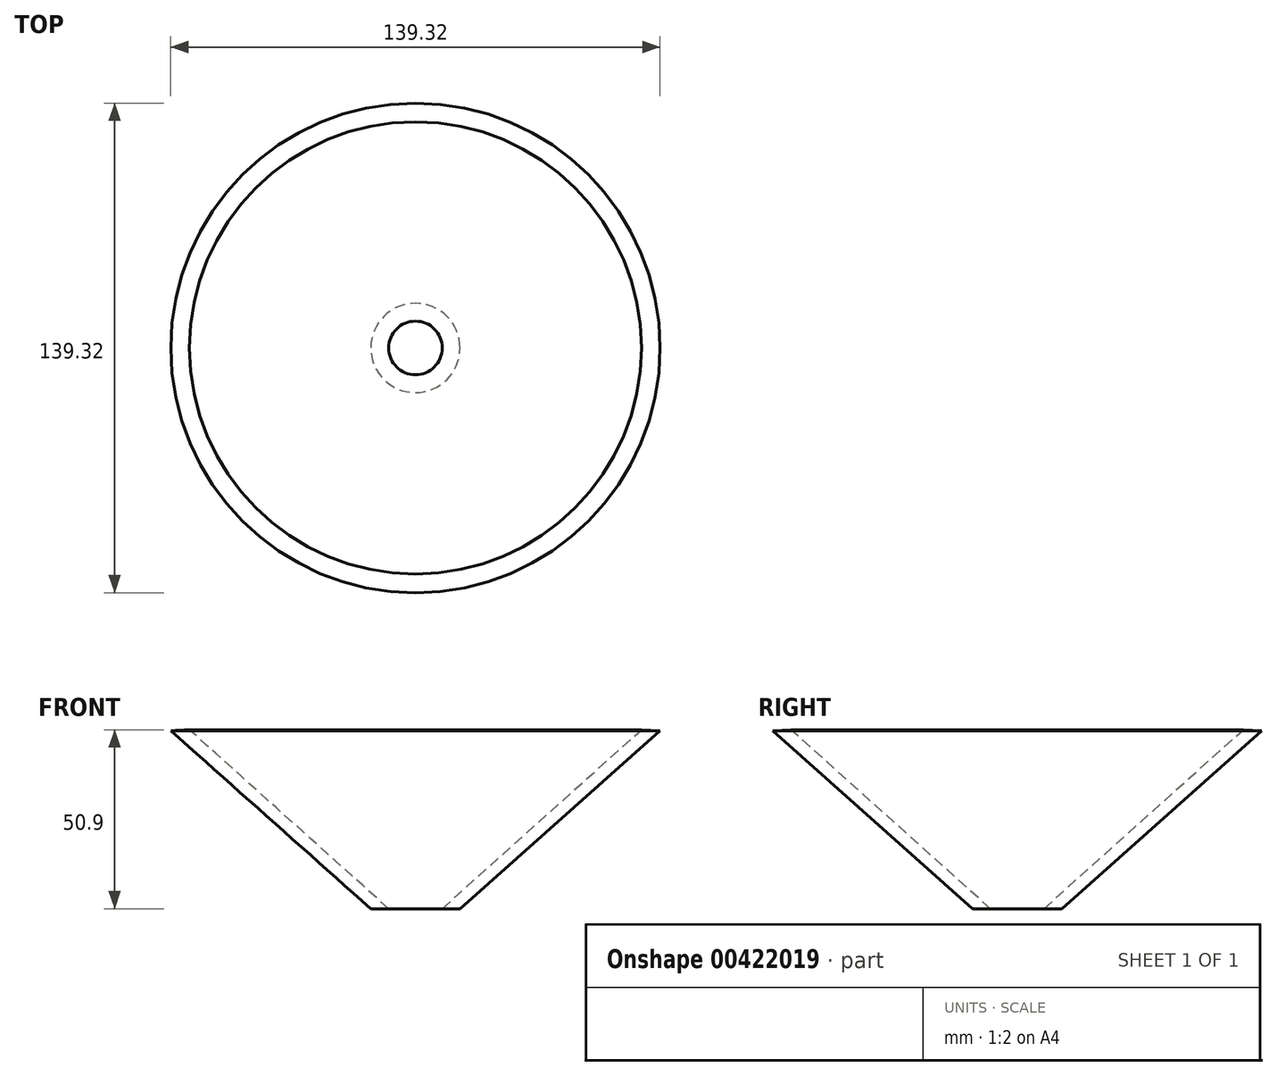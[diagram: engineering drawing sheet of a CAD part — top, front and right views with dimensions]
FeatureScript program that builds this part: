
annotation { "Feature Type Name" : "Feature", "Feature Type Description" : "" }
export const myFeature = defineFeature(function(context is Context, id is Id, definition is map)
    precondition{}
    {
        {
            var Q0;
            Q0=qCreatedBy(makeId("Front.planeOp"),FACE);
            var sketch = newSketch(context, id + "F0", { "sketchPlane" : qUnion([Q0])});
            skLineSegment(sketch, "E0", {"start": v(0, 0) * mm, "end": v(0, 25.4) * mm});
            skLineSegment(sketch, "E1", {"start": v(0, 25.4) * mm, "end": v(56.96, 76.02) * mm});
            skLineSegment(sketch, "E2", {"start": v(0, 0) * mm, "end": v(-12.7, 0) * mm});
            skLineSegment(sketch, "E3", {"start": v(-12.7, 0) * mm, "end": v(-12.7, 25.4) * mm});
            skLineSegment(sketch, "E4", {"start": v(-12.7, 25.4) * mm, "end": v(-5.08, 25.4) * mm});
            skLineSegment(sketch, "E5", {"start": v(-5.08, 25.4) * mm, "end": v(51.63, 76.3) * mm});
            skLineSegment(sketch, "E6", {"start": v(51.63, 76.3) * mm, "end": v(56.96, 76.02) * mm});
            skSolve(sketch);
        }
        {
            var Q0;
            Q0 = qSketchRegion(id + "F0", true);
            var Q1;
            Q1=sQuery(id+"F0.wireOp",EDGE,"E3");
            revolve(context, id + "F1", {"entities" : qUnion([Q0]), "axis" : qUnion([Q1]), "revolveType" : RevolveType.FULL});
        }
        {
            var Q0;
            Q0=makeQuery(id+"F1.opRevolve","SWEPT_FACE",FACE,{"disambiguationData":[OSD([sQuery(id+"F0.wireOp",EDGE,"E2")])]});
            extrude(context, id + "F2", {"entities" : qUnion([Q0]), "operationType" : NewBodyOperationType.REMOVE, "oppositeDirection" : true, "depth" : 25.4 * mm});
        }
    });
